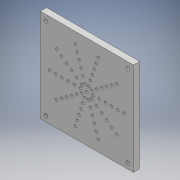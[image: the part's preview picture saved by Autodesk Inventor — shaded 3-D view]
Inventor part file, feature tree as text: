
AUTODESK INVENTOR PART (.ipt)
format: ipt  version: 2018 (Build 220112000, 112)  size: 293,376 bytes
history: native  units: mm
features: extrude x3, sketch x3, pattern_linear x2, pattern_circular x1
ambient origin geometry x8: Origin, YZ Plane, XZ Plane, XY Plane, X Axis, Y Axis, Z Axis, Center Point
bodies: Solid1 (feature_tree)
feature tree (9):
  extrude  "Extrusion1"  Depth=150.0mm
  extrude  "Extrusion2"  Depth=10.0mm
  pattern_linear  "Rectangular Pattern1"  Count1=7 Spacing1=10.0mm
  pattern_circular  "Circular Pattern1"  Count=7  [1 undecoded]
  extrude  "Extrusion3"  Depth=10.0mm TaperAngle=360.0deg
  pattern_linear  "Rectangular Pattern2"  Spacing1=12.5mm  [1 undecoded]
  sketch  "Sketch1"  dims[d0=150.0mm d1=150.0mm]
  sketch  "Sketch2"  dims[d2=10.0mm d3=0.0mm d4=4.0mm]
  sketch  "Sketch3"  dims[d5=10.0mm d6=0.0mm d7=70.0mm d9=10.0mm d10=70.0mm d12=10.0mm d13=100.0mm d14=360.0deg d16=12.5mm d17=135.0deg d18=10.0mm d19=0.0mm d20=20.0mm d22=132.0mm d23=20.0mm d25=132.0mm]
note: 2 required parameter values undecoded (feature->parameter linkage not recoverable at this tier; creation-order binding heuristic only, values carry confidence <= 0.55)
